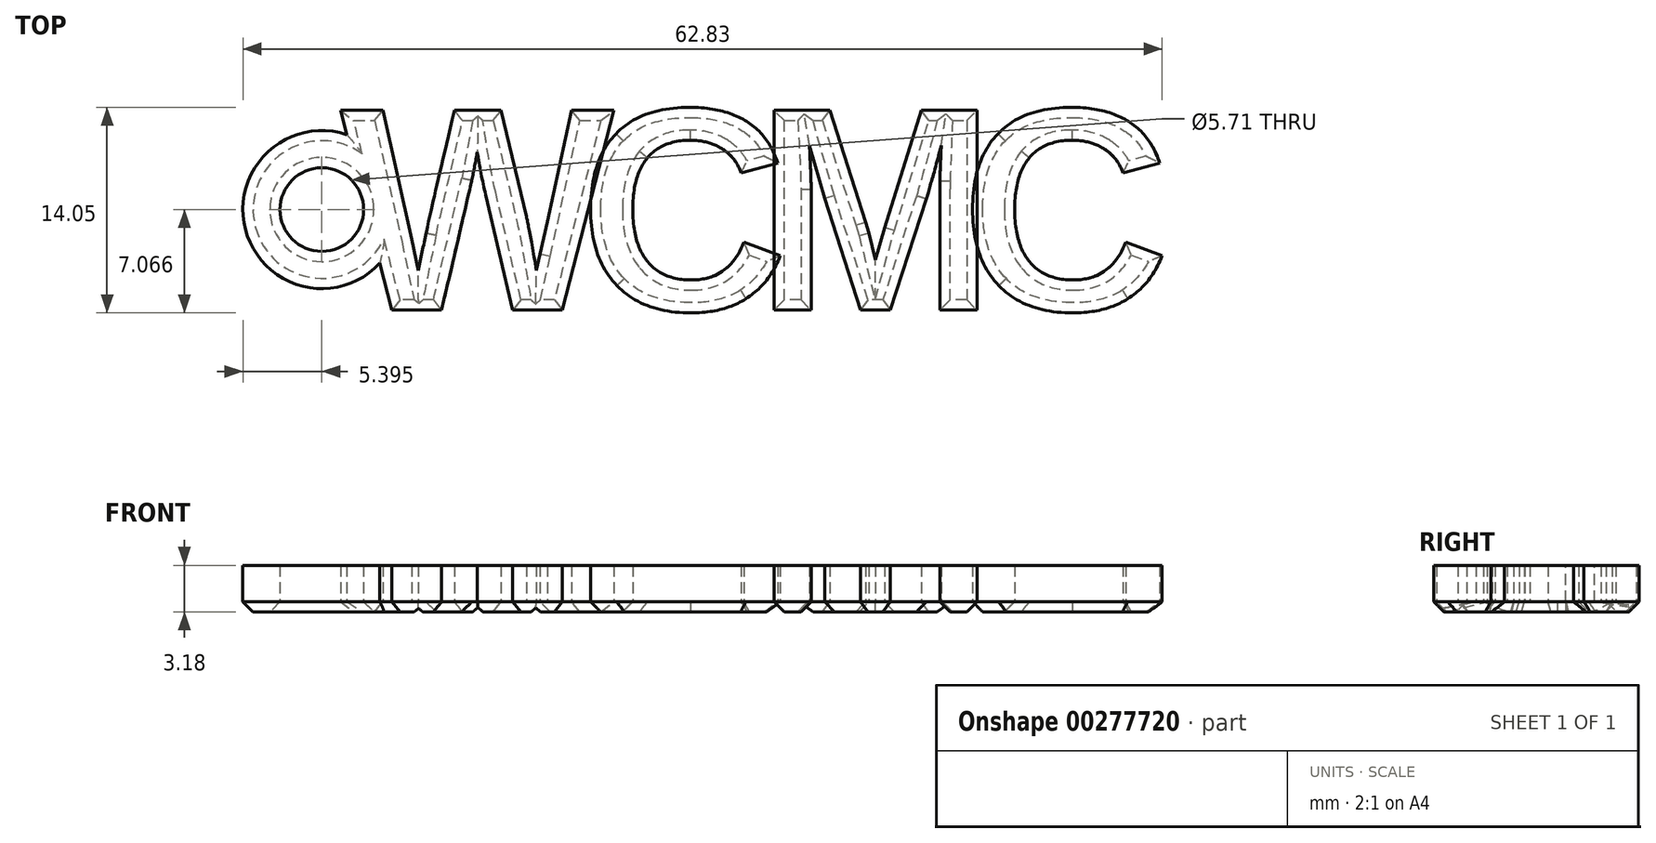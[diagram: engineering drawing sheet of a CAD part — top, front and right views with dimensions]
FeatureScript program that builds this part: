
annotation { "Feature Type Name" : "Feature", "Feature Type Description" : "" }
export const myFeature = defineFeature(function(context is Context, id is Id, definition is map)
    precondition{}
    {
        {
            var Q0;
            Q0=qCreatedBy(makeId("Top.planeOp"),FACE);
            var sketch = newSketch(context, id + "F0", { "sketchPlane" : qUnion([Q0])});
            skText(sketch, "E0", { "text": "W", "fontName": "Arimo-Bold.ttf"});
            skCircle(sketch, "E1", {"center": v(-1.25, -7.41) * mm, "radius": 5.4 * mm});
            skCircle(sketch, "E2", {"center": v(-1.25, -7.41) * mm, "radius": 2.86 * mm});
            const initialGuessF0  = {"E0": [0, -0.01429, 1, 0, 0.01429]};
            skSetInitialGuess(sketch, initialGuessF0);
            skSolve(sketch);
        }
        {
            var Q0;
            Q0=qCreatedBy(makeId("Top.planeOp"),FACE);
            var sketch = newSketch(context, id + "F1", { "sketchPlane" : qUnion([Q0])});
            skText(sketch, "E3", { "text": "C", "fontName": "Arimo-Bold.ttf"});
            const initialGuessF1  = {"E3": [0.0163, -0.01428, 1, 0, 0.01428]};
            skSetInitialGuess(sketch, initialGuessF1);
            skSolve(sketch);
        }
        {
            var Q0;
            Q0=qCreatedBy(makeId("Top.planeOp"),FACE);
            var sketch = newSketch(context, id + "F2", { "sketchPlane" : qUnion([Q0])});
            skText(sketch, "E4", { "text": "M", "fontName": "Arimo-Bold.ttf"});
            const initialGuessF2  = {"E4": [0.02832, -0.01428, 1, 0, 0.01428]};
            skSetInitialGuess(sketch, initialGuessF2);
            skSolve(sketch);
        }
        {
            var Q0;
            Q0=qCreatedBy(makeId("Top.planeOp"),FACE);
            var sketch = newSketch(context, id + "F3", { "sketchPlane" : qUnion([Q0])});
            skText(sketch, "E5", { "text": "C", "fontName": "Arimo-Bold.ttf"});
            const initialGuessF3  = {"E5": [0.0424, -0.01428, 1, 0, 0.01428]};
            skSetInitialGuess(sketch, initialGuessF3);
            skSolve(sketch);
        }
        {
            var Q0;
            Q0 = qSketchRegion(id + "F0", true);
            var Q1;
            Q1 = qSketchRegion(id + "F1", true);
            var Q2;
            Q2 = qSketchRegion(id + "F2", true);
            var Q3;
            Q3 = qSketchRegion(id + "F3", true);
            extrude(context, id + "F4", {"entities" : qUnion([Q0, Q1, Q2, Q3]), "depth" : 3.17 * mm});
        }
        {
            var Q0;
            Q0=makeQuery(id+"F4.opExtrude","CAP_FACE",FACE,{"disambiguationData":[OSD([sQuery(id+"F2.wireOp",EDGE,"E4.sketch_text.stroke-0"),sQuery(id+"F2.wireOp",EDGE,"E4.sketch_text.stroke-1"),sQuery(id+"F2.wireOp",EDGE,"E4.sketch_text.stroke-2"),sQuery(id+"F2.wireOp",EDGE,"E4.sketch_text.stroke-3"),sQuery(id+"F2.wireOp",EDGE,"E4.sketch_text.stroke-4"),sQuery(id+"F2.wireOp",EDGE,"E4.sketch_text.stroke-5"),sQuery(id+"F2.wireOp",EDGE,"E4.sketch_text.stroke-6"),sQuery(id+"F2.wireOp",EDGE,"E4.sketch_text.stroke-7"),sQuery(id+"F2.wireOp",EDGE,"E4.sketch_text.stroke-8"),sQuery(id+"F2.wireOp",EDGE,"E4.sketch_text.stroke-9"),sQuery(id+"F2.wireOp",EDGE,"E4.sketch_text.stroke-10"),sQuery(id+"F2.wireOp",EDGE,"E4.sketch_text.stroke-11"),sQuery(id+"F2.wireOp",EDGE,"E4.sketch_text.stroke-12"),sQuery(id+"F2.wireOp",EDGE,"E4.sketch_text.stroke-13"),sQuery(id+"F2.wireOp",EDGE,"E4.sketch_text.stroke-14"),sQuery(id+"F2.wireOp",EDGE,"E4.sketch_text.stroke-15"),sQuery(id+"F2.wireOp",EDGE,"E4.sketch_text.stroke-16"),sQuery(id+"F2.wireOp",EDGE,"E4.sketch_text.stroke-17"),sQuery(id+"F2.wireOp",EDGE,"E4.sketch_text.stroke-18"),sQuery(id+"F2.wireOp",EDGE,"E4.sketch_text.stroke-19"),sQuery(id+"F2.wireOp",EDGE,"E4.sketch_text.stroke-20")])],"isStart":true});
            var Q1;
            Q1=makeQuery(id+"F4.opExtrude","CAP_FACE",FACE,{"disambiguationData":[OSD([sQuery(id+"F1.wireOp",EDGE,"E3.sketch_text.stroke-0"),sQuery(id+"F1.wireOp",EDGE,"E3.sketch_text.stroke-1"),sQuery(id+"F1.wireOp",EDGE,"E3.sketch_text.stroke-2"),sQuery(id+"F1.wireOp",EDGE,"E3.sketch_text.stroke-3"),sQuery(id+"F1.wireOp",EDGE,"E3.sketch_text.stroke-4"),sQuery(id+"F1.wireOp",EDGE,"E3.sketch_text.stroke-5"),sQuery(id+"F1.wireOp",EDGE,"E3.sketch_text.stroke-6"),sQuery(id+"F1.wireOp",EDGE,"E3.sketch_text.stroke-7"),sQuery(id+"F1.wireOp",EDGE,"E3.sketch_text.stroke-8"),sQuery(id+"F1.wireOp",EDGE,"E3.sketch_text.stroke-9"),sQuery(id+"F1.wireOp",EDGE,"E3.sketch_text.stroke-10"),sQuery(id+"F1.wireOp",EDGE,"E3.sketch_text.stroke-11"),sQuery(id+"F1.wireOp",EDGE,"E3.sketch_text.stroke-12"),sQuery(id+"F1.wireOp",EDGE,"E3.sketch_text.stroke-13"),sQuery(id+"F1.wireOp",EDGE,"E3.sketch_text.stroke-14"),sQuery(id+"F1.wireOp",EDGE,"E3.sketch_text.stroke-15"),sQuery(id+"F1.wireOp",EDGE,"E3.sketch_text.stroke-16")])],"isStart":true});
            var Q2;
            Q2=makeQuery(id+"F4.opExtrude","CAP_FACE",FACE,{"disambiguationData":[OSD([sQuery(id+"F3.wireOp",EDGE,"E5.sketch_text.stroke-0"),sQuery(id+"F3.wireOp",EDGE,"E5.sketch_text.stroke-1"),sQuery(id+"F3.wireOp",EDGE,"E5.sketch_text.stroke-2"),sQuery(id+"F3.wireOp",EDGE,"E5.sketch_text.stroke-3"),sQuery(id+"F3.wireOp",EDGE,"E5.sketch_text.stroke-4"),sQuery(id+"F3.wireOp",EDGE,"E5.sketch_text.stroke-5"),sQuery(id+"F3.wireOp",EDGE,"E5.sketch_text.stroke-6"),sQuery(id+"F3.wireOp",EDGE,"E5.sketch_text.stroke-7"),sQuery(id+"F3.wireOp",EDGE,"E5.sketch_text.stroke-8"),sQuery(id+"F3.wireOp",EDGE,"E5.sketch_text.stroke-9"),sQuery(id+"F3.wireOp",EDGE,"E5.sketch_text.stroke-10"),sQuery(id+"F3.wireOp",EDGE,"E5.sketch_text.stroke-11"),sQuery(id+"F3.wireOp",EDGE,"E5.sketch_text.stroke-12"),sQuery(id+"F3.wireOp",EDGE,"E5.sketch_text.stroke-13"),sQuery(id+"F3.wireOp",EDGE,"E5.sketch_text.stroke-14"),sQuery(id+"F3.wireOp",EDGE,"E5.sketch_text.stroke-15"),sQuery(id+"F3.wireOp",EDGE,"E5.sketch_text.stroke-16")])],"isStart":true});
            var Q3;
            Q3=makeQuery(id+"F4.opExtrude","CAP_FACE",FACE,{"disambiguationData":[OSD([sQuery(id+"F0.wireOp",EDGE,"E0.sketch_text.stroke-0"),sQuery(id+"F0.wireOp",EDGE,"E0.sketch_text.stroke-1"),sQuery(id+"F0.wireOp",EDGE,"E0.sketch_text.stroke-2"),sQuery(id+"F0.wireOp",EDGE,"E0.sketch_text.stroke-3"),sQuery(id+"F0.wireOp",EDGE,"E0.sketch_text.stroke-4"),sQuery(id+"F0.wireOp",EDGE,"E0.sketch_text.stroke-5"),sQuery(id+"F0.wireOp",EDGE,"E0.sketch_text.stroke-6"),sQuery(id+"F0.wireOp",EDGE,"E0.sketch_text.stroke-7"),sQuery(id+"F0.wireOp",EDGE,"E0.sketch_text.stroke-8"),sQuery(id+"F0.wireOp",EDGE,"E0.sketch_text.stroke-9"),sQuery(id+"F0.wireOp",EDGE,"E0.sketch_text.stroke-10"),sQuery(id+"F0.wireOp",EDGE,"E0.sketch_text.stroke-11"),sQuery(id+"F0.wireOp",EDGE,"E0.sketch_text.stroke-12"),sQuery(id+"F0.wireOp",EDGE,"E0.sketch_text.stroke-13"),sQuery(id+"F0.wireOp",EDGE,"E0.sketch_text.stroke-14"),sQuery(id+"F0.wireOp",EDGE,"E0.sketch_text.stroke-15"),sQuery(id+"F0.wireOp",EDGE,"E0.sketch_text.stroke-16"),sQuery(id+"F0.wireOp",EDGE,"E0.sketch_text.stroke-17"),sQuery(id+"F0.wireOp",EDGE,"E0.sketch_text.stroke-18"),sQuery(id+"F0.wireOp",EDGE,"E0.sketch_text.stroke-19"),sQuery(id+"F0.wireOp",EDGE,"E1"),sQuery(id+"F0.wireOp",EDGE,"E2")])],"isStart":true});
            chamfer(context, id + "F5", {"entities" : qUnion([Q0, Q1, Q2, Q3]), "width" : 0.7 * mm, "tangentPropagation" : true});
        }
    });
